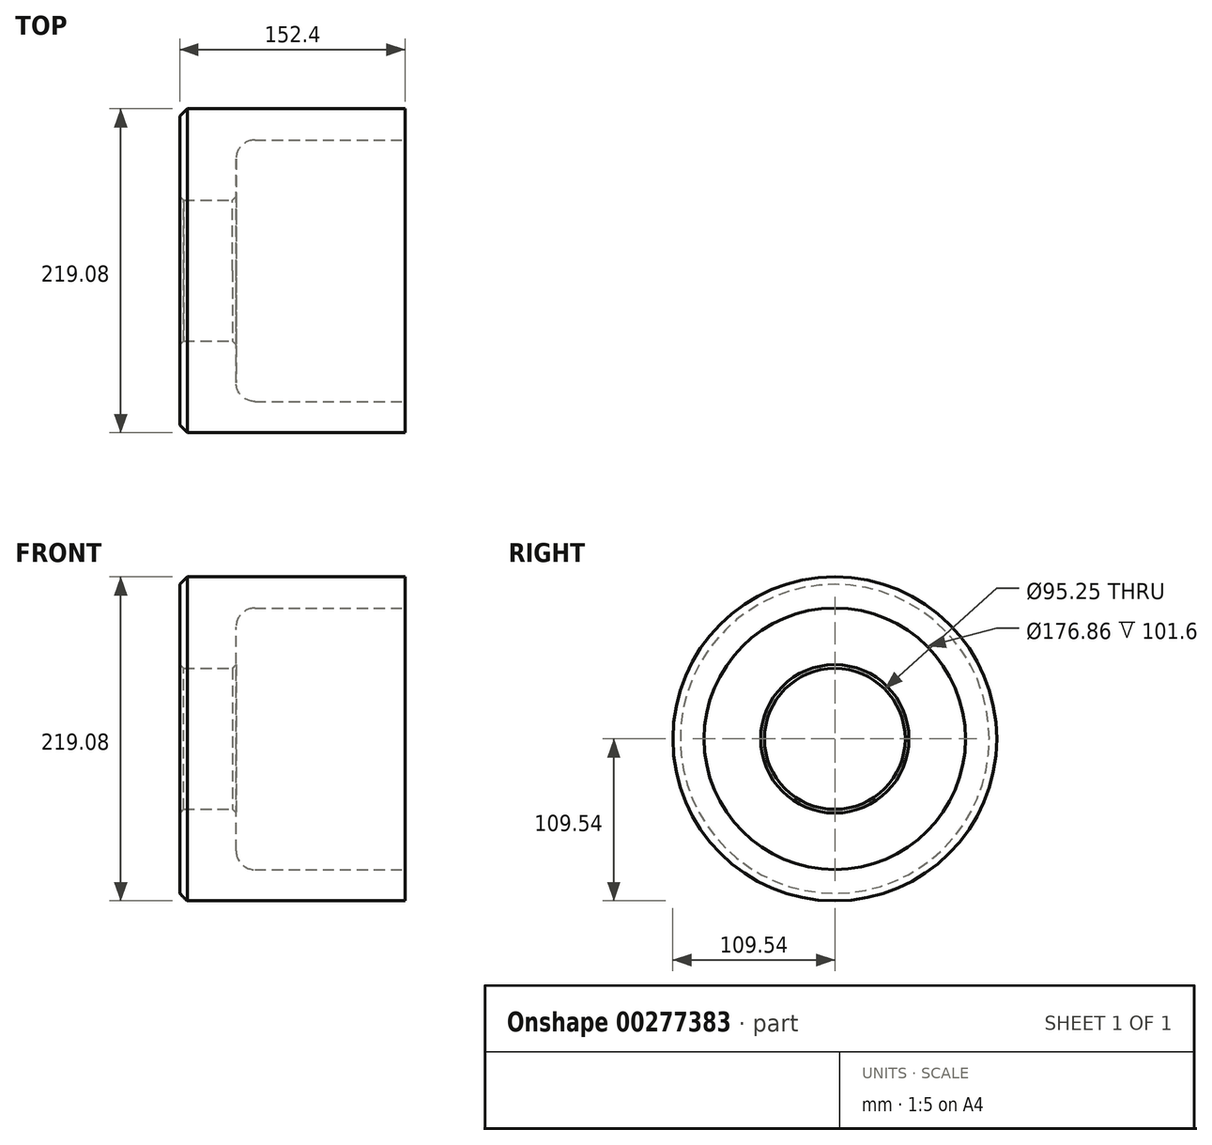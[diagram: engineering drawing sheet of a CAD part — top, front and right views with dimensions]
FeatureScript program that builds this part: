
annotation { "Feature Type Name" : "Feature", "Feature Type Description" : "" }
export const myFeature = defineFeature(function(context is Context, id is Id, definition is map)
    precondition{}
    {
        {
            var Q0;
            Q0=qCreatedBy(makeId("Front.planeOp"),FACE);
            var sketch = newSketch(context, id + "F0", { "sketchPlane" : qUnion([Q0])});
            skLineSegment(sketch, "E0", {"start": v(38.12, 0) * mm, "end": v(-161.1, 0) * mm, "construction": true});
            skLineSegment(sketch, "E1", {"start": v(0, 109.54) * mm, "end": v(0, 88.43) * mm});
            skLineSegment(sketch, "E2", {"start": v(0, 88.43) * mm, "end": v(-101.6, 88.43) * mm});
            skLineSegment(sketch, "E3", {"start": v(-114.3, 75.73) * mm, "end": v(-114.3, 47.62) * mm});
            skLineSegment(sketch, "E4", {"start": v(-114.3, 47.62) * mm, "end": v(-152.4, 47.62) * mm});
            skLineSegment(sketch, "E5", {"start": v(-152.4, 47.63) * mm, "end": v(-152.4, 109.54) * mm});
            skLineSegment(sketch, "E6", {"start": v(-152.4, 109.54) * mm, "end": v(0, 109.54) * mm});
            skPoint(sketch, "E7.visualSharp", {"position": v(-114.3, 88.43) * mm});
            skArc(sketch, "E7.filletArc", {"start": v(-101.6, 88.43) * mm, "mid": v(-110.58, 84.71) * mm, "end": v(-114.3, 75.73) * mm});
            skSolve(sketch);
        }
        {
            var Q0;
            Q0=makeQuery(id+"F0.imprint","IMPRINT",FACE,{"disambiguationData":[TD([[makeQuery(id+"F0.imprint","IMPRINT",EDGE,{"derivedFrom":sQuery(id+"F0.wireOp",EDGE,"E1")}),-1.0]])]});
            var Q1;
            Q1=sQuery(id+"F0.wireOp",EDGE,"E0");
            revolve(context, id + "F1", {"entities" : qUnion([Q0]), "axis" : qUnion([Q1]), "revolveType" : RevolveType.FULL});
        }
        {
            var Q0;
            Q0=makeQuery(id+"F1.opRevolve","SWEPT_EDGE",EDGE,{"disambiguationData":[OSD([sQuery(id+"F0.wireOp",EDGE,"E5"),sQuery(id+"F0.wireOp",EDGE,"E6")])]});
            chamfer(context, id + "F2", {"entities" : qUnion([Q0]), "width" : 5.08 * mm, "tangentPropagation" : true});
        }
        {
            var Q0;
            Q0=makeQuery(id+"F1.opRevolve","SWEPT_FACE",FACE,{"disambiguationData":[OSD([sQuery(id+"F0.wireOp",EDGE,"E4")])]});
            chamfer(context, id + "F3", {"entities" : qUnion([Q0]), "width" : 2.54 * mm, "tangentPropagation" : true});
        }
    });
